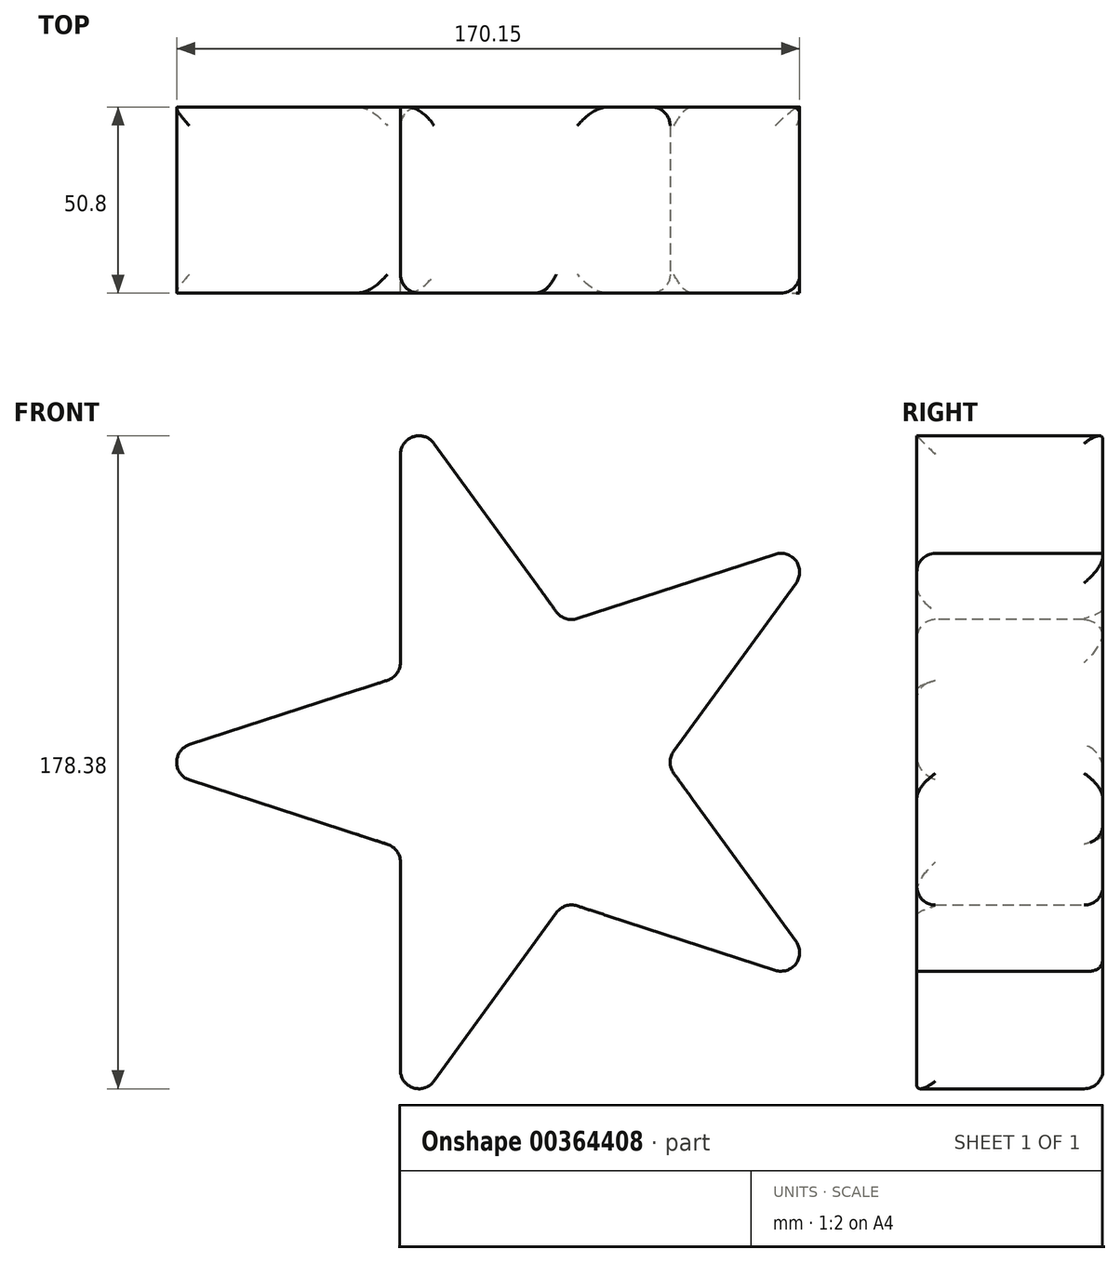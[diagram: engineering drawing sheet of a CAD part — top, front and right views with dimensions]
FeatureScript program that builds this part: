
annotation { "Feature Type Name" : "Feature", "Feature Type Description" : "" }
export const myFeature = defineFeature(function(context is Context, id is Id, definition is map)
    precondition{}
    {
        {
            var Q0;
            Q0=qCreatedBy(makeId("Front.planeOp"),FACE);
            var sketch = newSketch(context, id + "F0", { "sketchPlane" : qUnion([Q0])});
            skLineSegment(sketch, "E0", {"start": v(0, 0) * mm, "end": v(44.79, 61.65) * mm});
            skLineSegment(sketch, "E1", {"start": v(-27.68, 38.1) * mm, "end": v(44.79, 61.65) * mm});
            skLineSegment(sketch, "E2", {"start": v(-27.68, 38.1) * mm, "end": v(-72.47, 99.75) * mm});
            skLineSegment(sketch, "E3", {"start": v(-72.47, 99.75) * mm, "end": v(-72.47, 23.55) * mm});
            skLineSegment(sketch, "E4", {"start": v(-72.47, 23.55) * mm, "end": v(-144.94, 0) * mm});
            skLineSegment(sketch, "E5", {"start": v(-72.47, -23.55) * mm, "end": v(-144.94, 0) * mm});
            skLineSegment(sketch, "E6", {"start": v(-72.47, -99.75) * mm, "end": v(-72.47, -23.55) * mm});
            skLineSegment(sketch, "E7", {"start": v(-27.68, -38.1) * mm, "end": v(-72.47, -99.75) * mm});
            skLineSegment(sketch, "E8", {"start": v(44.79, -61.65) * mm, "end": v(-27.68, -38.1) * mm});
            skLineSegment(sketch, "E9", {"start": v(0, 0) * mm, "end": v(44.79, -61.65) * mm});
            skSolve(sketch);
        }
        {
            var Q0;
            Q0 = qSketchRegion(id + "F0", true);
            extrude(context, id + "F1", {"entities" : qUnion([Q0]), "oppositeDirection" : true, "depth" : 50.8 * mm, "hasSecondDirectionDraft" : true, "secondDirectionDraftAngle" : 3 * degree});
        }
        {
            var Q0;
            Q0=makeQuery(id+"F1.opExtrude","SWEPT_EDGE",EDGE,{"disambiguationData":[OSD([sQuery(id+"F0.wireOp",EDGE,"E2"),sQuery(id+"F0.wireOp",EDGE,"E3")])]});
            var Q1;
            Q1=makeQuery(id+"F1.opExtrude","SWEPT_EDGE",EDGE,{"disambiguationData":[OSD([sQuery(id+"F0.wireOp",EDGE,"E4"),sQuery(id+"F0.wireOp",EDGE,"E5")])]});
            var Q2;
            Q2=makeQuery(id+"F1.opExtrude","SWEPT_EDGE",EDGE,{"disambiguationData":[OSD([sQuery(id+"F0.wireOp",EDGE,"E0"),sQuery(id+"F0.wireOp",EDGE,"E1")])]});
            var Q3;
            Q3=makeQuery(id+"F1.opExtrude","SWEPT_EDGE",EDGE,{"disambiguationData":[OSD([sQuery(id+"F0.wireOp",EDGE,"E8"),sQuery(id+"F0.wireOp",EDGE,"E9")])]});
            var Q4;
            Q4=makeQuery(id+"F1.opExtrude","SWEPT_EDGE",EDGE,{"disambiguationData":[OSD([sQuery(id+"F0.wireOp",EDGE,"E6"),sQuery(id+"F0.wireOp",EDGE,"E7")])]});
            var Q5;
            Q5=makeQuery(id+"F1.opExtrude","CAP_EDGE",EDGE,{"disambiguationData":[OSD([sQuery(id+"F0.wireOp",EDGE,"E6")])],"isStart":false});
            var Q6;
            Q6=makeQuery(id+"F1.opExtrude","CAP_EDGE",EDGE,{"disambiguationData":[OSD([sQuery(id+"F0.wireOp",EDGE,"E7")])],"isStart":false});
            var Q7;
            Q7=makeQuery(id+"F1.opExtrude","CAP_EDGE",EDGE,{"disambiguationData":[OSD([sQuery(id+"F0.wireOp",EDGE,"E8")])],"isStart":false});
            var Q8;
            Q8=makeQuery(id+"F1.opExtrude","SWEPT_EDGE",EDGE,{"disambiguationData":[OSD([sQuery(id+"F0.wireOp",EDGE,"E7"),sQuery(id+"F0.wireOp",EDGE,"E8")])]});
            var Q9;
            Q9=makeQuery(id+"F1.opExtrude","SWEPT_EDGE",EDGE,{"disambiguationData":[OSD([sQuery(id+"F0.wireOp",EDGE,"E5"),sQuery(id+"F0.wireOp",EDGE,"E6")])]});
            var Q10;
            Q10=makeQuery(id+"F1.opExtrude","CAP_EDGE",EDGE,{"disambiguationData":[OSD([sQuery(id+"F0.wireOp",EDGE,"E4")])],"isStart":false});
            var Q11;
            Q11=makeQuery(id+"F1.opExtrude","SWEPT_EDGE",EDGE,{"disambiguationData":[OSD([sQuery(id+"F0.wireOp",EDGE,"E3"),sQuery(id+"F0.wireOp",EDGE,"E4")])]});
            var Q12;
            Q12=makeQuery(id+"F1.opExtrude","CAP_EDGE",EDGE,{"disambiguationData":[OSD([sQuery(id+"F0.wireOp",EDGE,"E2")])],"isStart":false});
            var Q13;
            Q13=makeQuery(id+"F1.opExtrude","SWEPT_EDGE",EDGE,{"disambiguationData":[OSD([sQuery(id+"F0.wireOp",EDGE,"E1"),sQuery(id+"F0.wireOp",EDGE,"E2")])]});
            var Q14;
            Q14=makeQuery(id+"F1.opExtrude","CAP_EDGE",EDGE,{"disambiguationData":[OSD([sQuery(id+"F0.wireOp",EDGE,"E0")])],"isStart":false});
            var Q15;
            Q15=makeQuery(id+"F1.opExtrude","SWEPT_EDGE",EDGE,{"disambiguationData":[OSD([sQuery(id+"F0.wireOp",EDGE,"E0"),sQuery(id+"F0.wireOp",EDGE,"E9")])]});
            var Q16;
            Q16=makeQuery(id+"F1.opExtrude","CAP_EDGE",EDGE,{"disambiguationData":[OSD([sQuery(id+"F0.wireOp",EDGE,"E0")])],"isStart":true});
            var Q17;
            Q17=makeQuery(id+"F1.opExtrude","CAP_EDGE",EDGE,{"disambiguationData":[OSD([sQuery(id+"F0.wireOp",EDGE,"E1")])],"isStart":true});
            var Q18;
            Q18=makeQuery(id+"F1.opExtrude","CAP_EDGE",EDGE,{"disambiguationData":[OSD([sQuery(id+"F0.wireOp",EDGE,"E3")])],"isStart":true});
            var Q19;
            Q19=makeQuery(id+"F1.opExtrude","CAP_EDGE",EDGE,{"disambiguationData":[OSD([sQuery(id+"F0.wireOp",EDGE,"E5")])],"isStart":true});
            var Q20;
            Q20=makeQuery(id+"F1.opExtrude","CAP_EDGE",EDGE,{"disambiguationData":[OSD([sQuery(id+"F0.wireOp",EDGE,"E7")])],"isStart":true});
            fillet(context, id + "F2", {"entities" : qUnion([Q0, Q1, Q2, Q3, Q4, Q5, Q6, Q7, Q8, Q9, Q10, Q11, Q12, Q13, Q14, Q15, Q16, Q17, Q18, Q19, Q20]), "radius" : 5.08 * mm, "tangentPropagation" : true, "allowEdgeOverflow" : false});
        }
    });
